# Revit family: OASIS SH-4834 RSLS ABF
name_source: partatom
category: Plumbing Fixtures
revit_build: Autodesk Revit 2017 (Build: 20171027_0315(x64)
units: mm (PartAtom-declared; Revit-internal decimal feet)

## family parameters
Always vertical = Yes
Cut with Voids When Loaded = No
OmniClass Number = 23.45.05.14.21.11
OmniClass Title = Bath/Shower Units
Part Type = Normal
Room Calculation Point = No
Round Connector Dimension = Use Diameter
Shared = No
Work Plane-Based = No

## types (3) — shared parameters
BIM Model By = www.epoch-design.com
Bar_Horz_Center = 29"
Bar_Vert_Bottom = 4"
Cold Water Connector = Cold Water Connection
Color = <By Category>
Depth = 34"
Drain Clearance = 3"
Enclosure_Width = 44 11/16"
Flange = 1 1/4"
Grab Bar Finish = <By Category>
Grab Bar_Back to Side = 10 11/32"
Grab Bar_Side to Front = 6"
Grab Bar_Vertical to Front = 6"
Height = 76 1/2"
Hot Water Connector = Hot Water Connection
Manufacturer = OASIS
Radius_Fillet = 1/4"
Radius_Lower Wall Corner = 1 11/16"
Radius_Shelf_Elevation = 2"
Radius_Shelf_Inside Corner = 2 3/16"
Radius_Shelf_Outside Corner = 4"
Radius_Threshold_Bottom = 2"
Radius_Threshold_Top = 2 1/2"
Radius_Wall_Bottom = 1 9/16"
Radius_Wall_Corner = 4"
Sanitary Connector = Sanitary Connection
Sanitary Radius = 1 11/16"
Seat Finish = <By Category>
Seat_Height = 18"
Shelf Depth = 1 13/16"
Shelf_Height_High = 24 1/2"
Shelf_Height_Low = 11"
Shelf_Width = 15"
Stainless steel = <By Category>
Threshold_Depth = 3"
Threshold_Height = 6"
Type Comments = Shower
URL = www.oasisbath.com
Wall_Thickness = 1 21/32"
Width = 48"

## per-type parameters (varying)
| type | Bar_Horz_Back | Bar_Horz_Side | Bar_Vert | Model |
| ABF Base Model, 3SF, 3SM, FH  packages | No | No | No | SH-4834(RS,LS) ABF/(Base Model,3SF,3SM,FH) |
| ABF BP1 package | Yes | Yes | No | SH-4834(RS,LS) ABF/BP1 |
| ABF BP2 package | Yes | Yes | Yes | SH-4834(RS,LS) ABF/BP2 |

## geometry (parser evidence)
native form markers: Sweep x5
no freeform markers — native parametric forms only
